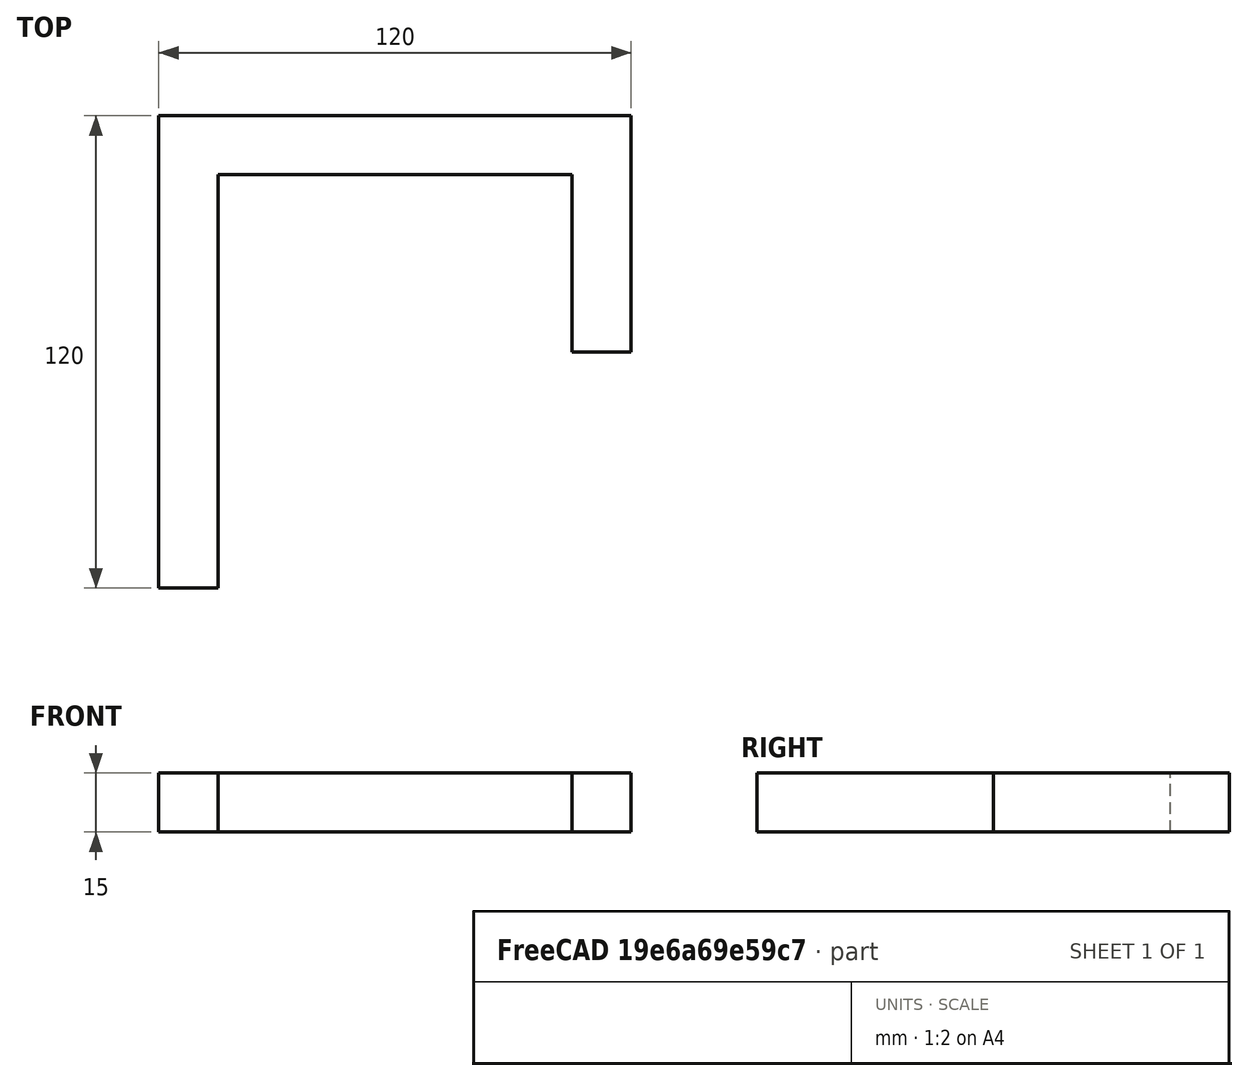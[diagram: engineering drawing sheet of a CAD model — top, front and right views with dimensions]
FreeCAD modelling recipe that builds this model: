
FCSTD DOCUMENT  (FreeCAD 0.20R29603 (Git))
Label: figureAssemblyV2
License: All rights reserved
LicenseURL: http://en.wikipedia.org/wiki/All_rights_reserved
objects: App::Link×6, App::DocumentObjectGroup×3, PartDesign::CoordinateSystem×2, Sketcher::SketchObject×1, PartDesign::Pad×1, PartDesign::Body×1, App::FeaturePython×1, App::Part×1
note: 6 computed .brp shape members not serialized (recipe doc carries the construction recipe); baked Part::Feature solids carry a one-line shape summary decoded from their .brp

FEATURE [Sketcher::SketchObject] Sketch009  label="tbaseSketch001"
  FullyConstrained = true
  MapMode = 5
  Support = -> [XY_Plane]
  sketch-geometry (8):
    g0: LineSegment StartX=-45 StartY=45 StartZ=0 EndX=45 EndY=45 EndZ=0
    g1: LineSegment StartX=45 StartY=45 StartZ=0 EndX=45 EndY=0 EndZ=0
    g2: LineSegment StartX=45 StartY=0 StartZ=0 EndX=60 EndY=0 EndZ=0
    g3: LineSegment StartX=60 StartY=0 StartZ=0 EndX=60 EndY=60 EndZ=0
    g4: LineSegment StartX=60 StartY=60 StartZ=0 EndX=-60 EndY=60 EndZ=0
    g5: LineSegment StartX=-60 StartY=60 StartZ=0 EndX=-60 EndY=-60 EndZ=0
    g6: LineSegment StartX=-45 StartY=45 StartZ=0 EndX=-45 EndY=-60 EndZ=0
    g7: LineSegment StartX=-45 StartY=-60 StartZ=0 EndX=-60 EndY=-60 EndZ=0
  constraints (23):
    c: Horizontal(g0)
    c: Coincident(g0,g1)
    c: Vertical(g1)
    c: Coincident(g1,g2)
    c: Coincident(g2,g3)
    c: Vertical(g3)
    c: Coincident(g3,g4)
    c: Horizontal(g4)
    c: Coincident(g4,g5)
    c: Vertical(g5)
    c: Distance(g0) = 90
    c: Distance(g2,g1) = 15
    c: Horizontal(g2)
    c: Coincident(g6,g0)
    c: Vertical(g6)
    c: Coincident(g7,g6)
    c: Coincident(g7,g5)
    c: Horizontal(g7)
    c: Distance(g7) = 15
    c: Symmetric(g3,g5,g-1)
    c: Distance(g3) = 60
    c: DistanceY(g5,g5) = 120
    c: DistanceY(g1,g1) = 45
FEATURE [PartDesign::Pad] Pad
  Direction = (0,0,1)
  Length = 15
  Length2 = 10
  Profile = -> Sketch009
  ReferenceAxis = -> Sketch009 [N_Axis]
  Type = 0
FEATURE [PartDesign::CoordinateSystem] LCS_1
  AttacherType = Attacher::AttachEngine3D
FEATURE [PartDesign::Body] Body
  Group = -> [Sketch009,Pad,LCS_1]
  Origin = -> Origin
  Tip = -> Pad
FEATURE [App::DocumentObjectGroup] Parts
  Group = -> [Body]
FEATURE [PartDesign::CoordinateSystem] LCS_Origin
  AttacherType = Attacher::AttachEngine3D
  MapMode = 2
  Support = -> [X_Axis001]
FEATURE [App::DocumentObjectGroup] Constraints
FEATURE [App::FeaturePython] Variables  # WARN: FeaturePython — macro-defined, semantics opaque (R4)
  Type = App::PropertyContainer
FEATURE [App::DocumentObjectGroup] Configurations
FEATURE [App::Link] Body001  label="bottom"
  AttachedBy = #LCS_1
  AttachedTo = Parent Assembly#LCS_Origin
  LinkedObject = -> Body
  SolverId = Asm4EE
  expr: Placement = LCS_Origin.Placement * AttachmentOffset * LCS_1.Placement ^ -1
FEATURE [App::Link] Body002  label="top"
  AttachedBy = #LCS_1
  AttachedTo = Body001#LCS_1
  AttachmentOffset = pos=(-60,60,165) rot=(0,0,-1;3.14159rad)
  LinkPlacement = pos=(-60,60,165) rot=(0,0,-1;3.14159rad)
  LinkedObject = -> Body
  Placement = pos=(-60,60,165) rot=(0,0,-1;3.14159rad)
  SolverId = Asm4EE
  expr: Placement = Body001.Placement * LCS_1.Placement * AttachmentOffset * LCS_1.Placement ^ -1
FEATURE [App::Link] Body003  label="left1"
  AttachedBy = #LCS_1
  AttachedTo = Parent Assembly#LCS_Origin
  AttachmentOffset = pos=(-60,-45,60) rot=(-0.57735,-0.57735,0.57735;4.18879rad)
  LinkPlacement = pos=(-60,-45,60) rot=(-0.57735,-0.57735,0.57735;4.18879rad)
  LinkedObject = -> Body
  Placement = pos=(-60,-45,60) rot=(-0.57735,-0.57735,0.57735;4.18879rad)
  SolverId = Asm4EE
  expr: Placement = LCS_Origin.Placement * AttachmentOffset * LCS_1.Placement ^ -1
FEATURE [App::Link] Body004  label="right2"
  AttachedBy = #LCS_1
  AttachedTo = Parent Assembly#LCS_Origin
  AttachmentOffset = pos=(45,60,60) rot=(0.57735,0.57735,0.57735;2.0944rad)
  LinkPlacement = pos=(45,60,60) rot=(0.57735,0.57735,0.57735;2.0944rad)
  LinkedObject = -> Body
  Placement = pos=(45,60,60) rot=(0.57735,0.57735,0.57735;2.0944rad)
  SolverId = Asm4EE
  expr: Placement = LCS_Origin.Placement * AttachmentOffset * LCS_1.Placement ^ -1
FEATURE [App::Link] Body005  label="left2"
  AttachedBy = #LCS_1
  AttachedTo = Parent Assembly#LCS_Origin
  AttachmentOffset = pos=(0,120,120) rot=(0.57735,-0.57735,0.57735;2.0944rad)
  LinkPlacement = pos=(0,120,120) rot=(0.57735,-0.57735,0.57735;2.0944rad)
  LinkedObject = -> Body
  Placement = pos=(0,120,120) rot=(0.57735,-0.57735,0.57735;2.0944rad)
  SolverId = Asm4EE
  expr: Placement = LCS_Origin.Placement * AttachmentOffset * LCS_1.Placement ^ -1
FEATURE [App::Link] Body006
  AttachedBy = #LCS_1
  AttachedTo = Parent Assembly#LCS_Origin
  AttachmentOffset = pos=(-120,0,120) rot=(0.57735,-0.57735,0.57735;4.18879rad)
  LinkPlacement = pos=(-120,0,120) rot=(0.57735,-0.57735,0.57735;4.18879rad)
  LinkedObject = -> Body
  Placement = pos=(-120,0,120) rot=(0.57735,-0.57735,0.57735;4.18879rad)
  SolverId = Asm4EE
  expr: Placement = LCS_Origin.Placement * AttachmentOffset * LCS_1.Placement ^ -1
FEATURE [App::Part] Assembly
  AssemblyType = Part::Link
  Group = -> [LCS_Origin,Constraints,Variables,Configurations,Body001,Body002,Body003,Body004,Body005,Body006]
  Origin = -> Origin001
  Type = Assembly
